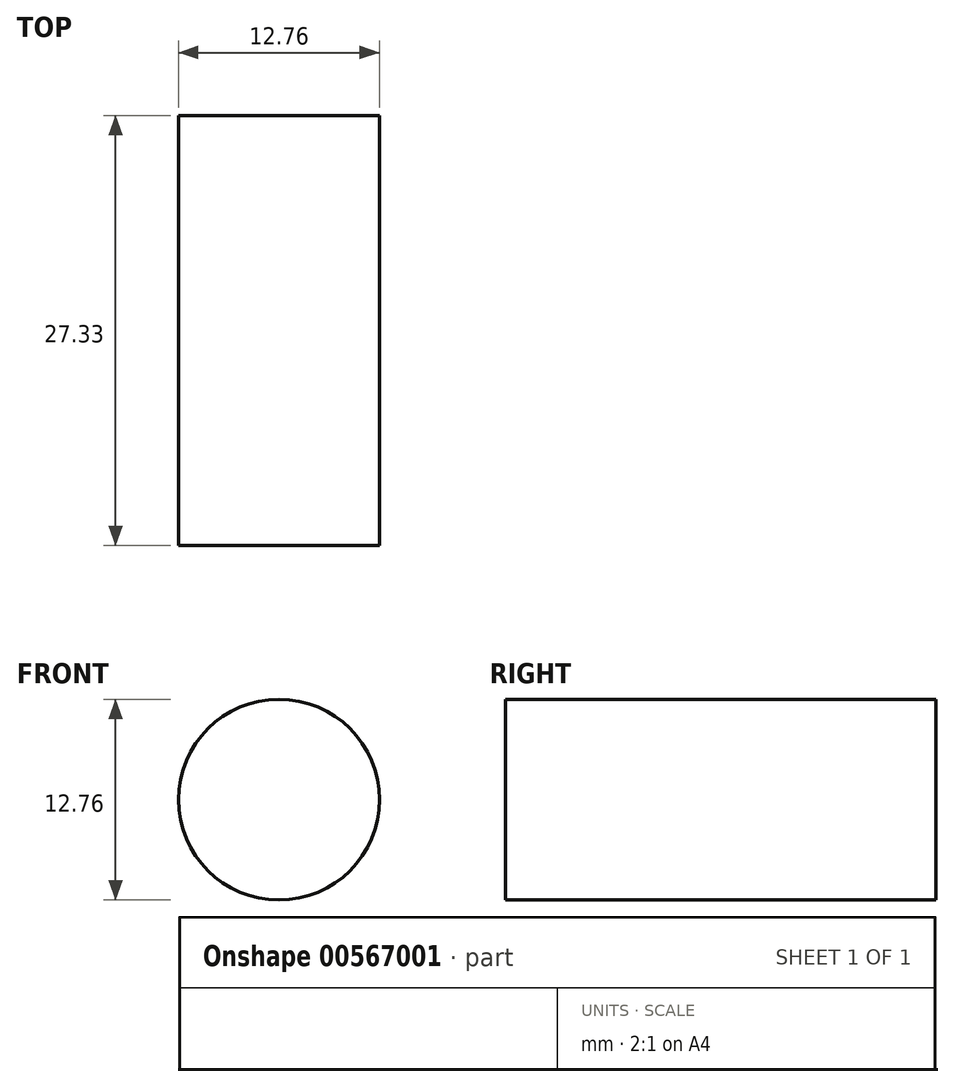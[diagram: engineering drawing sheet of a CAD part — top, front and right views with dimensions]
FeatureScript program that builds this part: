
annotation { "Feature Type Name" : "Feature", "Feature Type Description" : "" }
export const myFeature = defineFeature(function(context is Context, id is Id, definition is map)
    precondition{}
    {
        {
            var Q0;
            Q0=qCreatedBy(makeId("Front.planeOp"),FACE);
            var sketch = newSketch(context, id + "F0", { "sketchPlane" : qUnion([Q0])});
            skCircle(sketch, "E0", {"center": v(0, 0) * mm, "radius": 6.38 * mm});
            skSolve(sketch);
        }
        {
            var Q0;
            Q0 = qSketchRegion(id + "F0", true);
            extrude(context, id + "F1", {"entities" : qUnion([Q0]), "depth" : 27.33 * mm, "offsetDistance" : 25 * mm});
        }
    });
